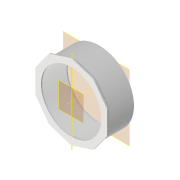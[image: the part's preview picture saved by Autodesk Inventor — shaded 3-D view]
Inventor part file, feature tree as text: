
AUTODESK INVENTOR PART (.ipt)
format: ipt  version: 2022 (Build 260153000, 153)  size: 609,280 bytes
history: native  units: in
note: dims shown in document units (in); Inventor stores cm internally (conversion verified against a paired STEP export)
features: other x9, reference x6, plane x3, extrude x2, sketch x2, fillet x1, chamfer x1
ambient origin geometry x8: Origin, YZ Plane, XZ Plane, XY Plane, X Axis, Y Axis, Z Axis, Center Point
bodies: Solid1 (feature_tree)
feature tree (24):
  plane  "Work Plane1"
  plane  "Arbeitsebene2"
  extrude  "Extrusion4"  Depth=0.0394in
  plane  "Arbeitsebene3"
  sketch  "Skizze5"  dims[d11=2.4409in d12=0.0394in d13=0.0137in]
  other  "Arbeitsachse1"
  other  "Arbeitsachse2"
  other  "Spirale1"
  extrude  "Extrusion5"  Depth=1.3056in
  fillet  "Rundung1"  [1 undecoded]
  chamfer  "Fase1"  Distance=0.0687in
  reference  "Referenz15"
  reference  "Referenz16"
  reference  "Referenz17"
  reference  "Referenz18"
  reference  "Referenz19"
  reference  "Referenz20"
  sketch  "Skizze6"  dims[d16=0.0591in d17=1.3056in d18=0.0in d19=0.0687in d20=0.0079in d21=0.0591in d22=1.0in d23=5.5118in d24=0.0in d25=90.0deg d26=90.0deg d27=0.0in d28=0.0in d29=2.3622in d30=0.0394in d31=0.0in d32=0.125in d33=0.0394in d34=0.125in d35=45.0deg]
  other  "<userpath>\Documents\GitHub\Matchboxscope\INVENTOR\Anglerfish_VCM_v2.iam"
  other  "Anglerfish_VCM_v2.iam"
  other  "Anglerfish_middle2_m12VCMLens_v2:1"
  other  "<userpath>\Documents\Matchboxscope\INVENTOR\Matchboxscope_v1.iam"
  other  "Matchboxscope_v1.iam"
  other  "Matchboxscope_middle2_v1:1"
note: 1 required parameter value undecoded (feature->parameter linkage not recoverable at this tier; creation-order binding heuristic only, values carry confidence <= 0.55)
